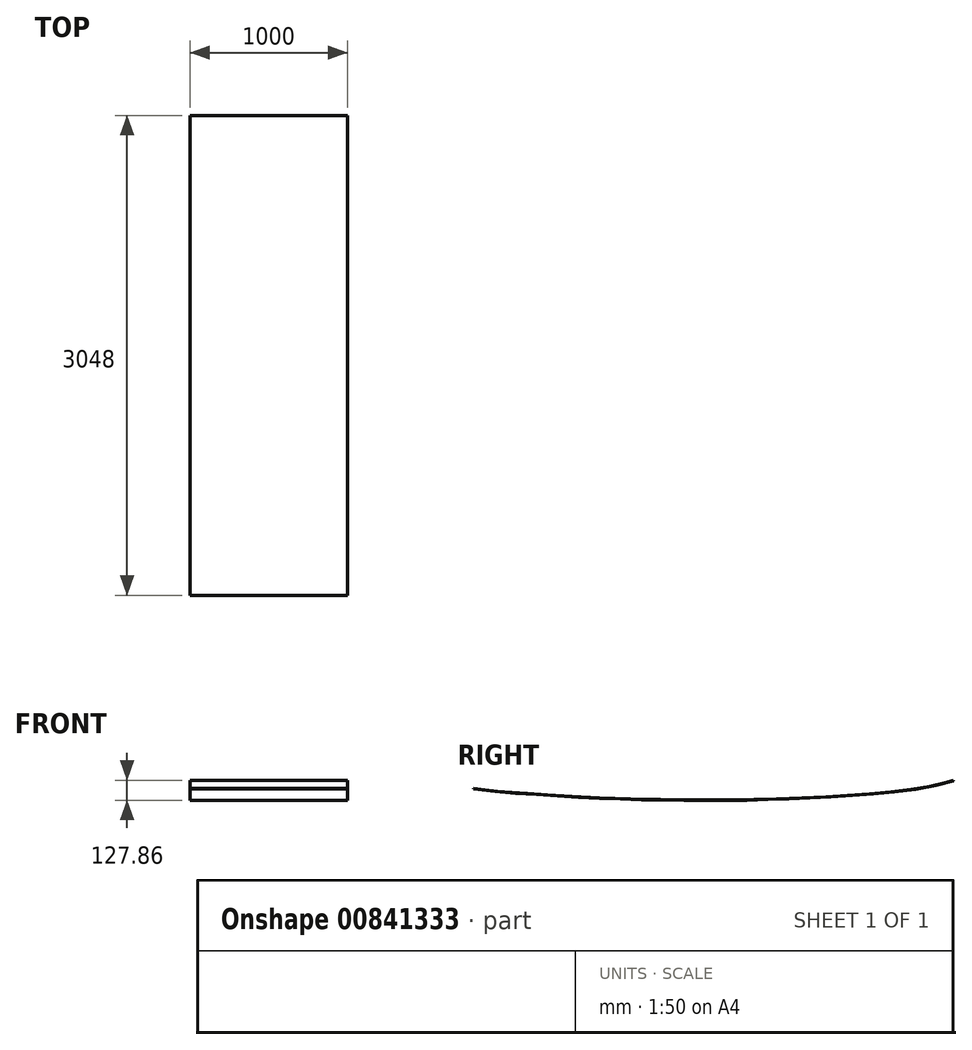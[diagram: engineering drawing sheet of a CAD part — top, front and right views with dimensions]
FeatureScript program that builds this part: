
annotation { "Feature Type Name" : "Feature", "Feature Type Description" : "" }
export const myFeature = defineFeature(function(context is Context, id is Id, definition is map)
    precondition{}
    {
        {
            var Q0;
            Q0=qCreatedBy(makeId("Right.planeOp"),FACE);
            var sketch = newSketch(context, id + "F0", { "sketchPlane" : qUnion([Q0])});
            skFitSpline(sketch, "E0", {"points": [v(-1524, 72) * mm, v(-1424, 61) * mm, v(-1324, 51) * mm, v(-1224, 43) * mm, v(-1124, 37) * mm, v(-1024, 30) * mm, v(-924, 24) * mm, v(-824, 19) * mm, v(-724, 14) * mm, v(-624, 10) * mm, v(-524, 7) * mm, v(-424, 4) * mm, v(-324, 2) * mm, v(-224, 1) * mm, v(-124, 0) * mm, v(-24, 0) * mm, v(76, 0) * mm, v(176, 1) * mm, v(276, 3) * mm, v(376, 6) * mm, v(476, 9) * mm, v(576, 13) * mm, v(676, 18) * mm, v(776, 24) * mm, v(876, 30) * mm, v(976, 38) * mm, v(1076, 47) * mm, v(1176, 57) * mm, v(1276, 70) * mm, v(1376, 86) * mm, v(1476, 110) * mm, v(1524, 125) * mm], "startDerivative": vector(44.76, -10.57) * mm, "endDerivative": vector(60.2, 24.67) * mm});
            skLineSegment(sketch, "E1", {"start": v(-1524, 0) * mm, "end": v(1524, 0) * mm, "construction": true});
            skLineSegment(sketch, "E2", {"start": v(1524, 125) * mm, "end": v(1523.54, 124.81) * mm, "construction": true});
            skPoint(sketch, "E3", {"position": v(1219, 0) * mm});
            skPoint(sketch, "E4", {"position": v(-1219, 0) * mm});
            skLineSegment(sketch, "E5", {"start": v(-1524, 72) * mm, "end": v(-1523.51, 71.89) * mm, "construction": true});
            skFitSpline(sketch, "E6.0", {"points": [v(-1525.26, 75.2) * mm, v(-1525.15, 75.2) * mm, v(-1524.92, 75.16) * mm, v(-1524.63, 75.12) * mm, v(-1524.4, 75.09) * mm, v(-1524.23, 75.06) * mm, v(-1524.06, 75.04) * mm, v(-1523.91, 75.02) * mm, v(-1523.8, 75) * mm, v(-1523.73, 75) * mm, v(-1523.67, 74.98) * mm, v(-1523.63, 74.98) * mm, v(-1523.6, 74.97) * mm, v(-1523.56, 74.97) * mm, v(-1523.55, 74.96) * mm, v(-1523.53, 74.96) * mm, v(-1523.53, 74.96) * mm, v(-1523.53, 74.96) * mm, v(-1523.51, 74.96) * mm, v(-1523.47, 74.95) * mm, v(-1523.39, 74.94) * mm, v(-1523.25, 74.93) * mm, v(-1523.04, 74.9) * mm, v(-1522.7, 74.86) * mm, v(-1522.28, 74.81) * mm, v(-1521.63, 74.74) * mm, v(-1520.65, 74.63) * mm, v(-1519.2, 74.46) * mm, v(-1517.5, 74.27) * mm, v(-1515.57, 74.05) * mm, v(-1512.68, 73.73) * mm, v(-1508.53, 73.27) * mm, v(-1502.8, 72.63) * mm, v(-1494.26, 71.68) * mm, v(-1482.18, 70.35) * mm, v(-1466.2, 68.6) * mm, v(-1452.33, 67.08) * mm, v(-1441.27, 65.88) * mm, v(-1433.11, 65) * mm, v(-1425.17, 64.14) * mm, v(-1417.55, 63.33) * mm, v(-1410.26, 62.55) * mm, v(-1403.27, 61.81) * mm, v(-1396.54, 61.1) * mm, v(-1387.88, 60.2) * mm, v(-1377.6, 59.15) * mm, v(-1365.91, 57.98) * mm, v(-1354.65, 56.87) * mm, v(-1343.62, 55.82) * mm, v(-1334.43, 54.96) * mm, v(-1326.98, 54.28) * mm, v(-1319.42, 53.6) * mm, v(-1309.75, 52.74) * mm, v(-1297.85, 51.7) * mm, v(-1285.7, 50.67) * mm, v(-1273.38, 49.66) * mm, v(-1260.92, 48.68) * mm, v(-1248.4, 47.73) * mm, v(-1235.85, 46.82) * mm, v(-1223.36, 45.96) * mm, v(-1210.96, 45.15) * mm, v(-1198.64, 44.4) * mm, v(-1182.3, 43.43) * mm, v(-1161.98, 42.28) * mm, v(-1141.73, 41.1) * mm, v(-1125.51, 40.1) * mm, v(-1109.26, 39.05) * mm, v(-1088.9, 37.64) * mm, v(-1064.41, 35.87) * mm, v(-1039.9, 34.1) * mm, v(-1015.42, 32.4) * mm, v(-990.96, 30.83) * mm, v(-958.36, 28.86) * mm, v(-917.61, 26.63) * mm, v(-876.83, 24.6) * mm, v(-844.19, 23) * mm, v(-811.54, 21.39) * mm, v(-770.75, 19.28) * mm, v(-721.82, 16.85) * mm, v(-672.88, 14.74) * mm, v(-623.94, 12.95) * mm, v(-574.98, 11.47) * mm, v(-526, 10.09) * mm, v(-477.03, 8.54) * mm, v(-428.07, 7.06) * mm, v(-379.12, 5.88) * mm, v(-338.32, 5.17) * mm, v(-305.68, 4.77) * mm, v(-281.2, 4.53) * mm, v(-256.7, 4.31) * mm, v(-232.22, 4.1) * mm, v(-207.72, 3.83) * mm, v(-183.23, 3.53) * mm, v(-158.75, 3.26) * mm, v(-134.27, 3.04) * mm, v(-109.79, 2.93) * mm, v(-85.3, 2.92) * mm, v(-60.82, 2.95) * mm, v(-36.33, 3) * mm, v(-11.83, 3) * mm, v(20.82, 2.96) * mm, v(53.47, 2.92) * mm, v(86.11, 3.03) * mm, v(118.75, 3.26) * mm, v(151.4, 3.64) * mm, v(184.04, 4.12) * mm, v(216.68, 4.66) * mm, v(249.32, 5.32) * mm, v(281.95, 6.15) * mm, v(306.43, 6.85) * mm, v(330.91, 7.6) * mm, v(355.4, 8.37) * mm, v(379.89, 9.12) * mm, v(412.54, 10.07) * mm, v(445.18, 11) * mm, v(477.81, 12.05) * mm, v(510.44, 13.22) * mm, v(543.07, 14.55) * mm, v(575.7, 15.98) * mm, v(608.33, 17.48) * mm, v(640.96, 19.08) * mm, v(673.57, 20.85) * mm, v(698.03, 22.28) * mm, v(722.5, 23.76) * mm, v(746.96, 25.26) * mm, v(771.43, 26.75) * mm, v(795.91, 28.16) * mm, v(820.38, 29.55) * mm, v(844.84, 30.98) * mm, v(869.3, 32.52) * mm, v(893.73, 34.24) * mm, v(918.16, 36.12) * mm, v(942.6, 38.13) * mm, v(967.04, 40.22) * mm, v(991.48, 42.37) * mm, v(1015.91, 44.54) * mm, v(1040.35, 46.75) * mm, v(1064.79, 48.98) * mm, v(1089.23, 51.23) * mm, v(1113.66, 53.52) * mm, v(1138.08, 55.92) * mm, v(1158.41, 58.05) * mm, v(1174.66, 59.86) * mm, v(1190.91, 61.75) * mm, v(1211.21, 64.25) * mm, v(1235.57, 67.43) * mm, v(1255.88, 70.2) * mm, v(1272.13, 72.48) * mm, v(1288.4, 74.78) * mm, v(1308.72, 77.73) * mm, v(1333.07, 81.49) * mm, v(1353.3, 84.87) * mm, v(1369.4, 87.79) * mm, v(1385.47, 90.86) * mm, v(1401.47, 94.18) * mm, v(1417.46, 97.78) * mm, v(1429.46, 100.62) * mm, v(1441.49, 103.62) * mm, v(1451.53, 106.26) * mm, v(1459.6, 108.45) * mm, v(1465.65, 110.14) * mm, v(1470.7, 111.59) * mm, v(1474.76, 112.76) * mm, v(1478.83, 113.96) * mm, v(1483.9, 115.47) * mm, v(1491.85, 117.88) * mm, v(1499.39, 120.22) * mm, v(1506.15, 122.36) * mm, v(1510.74, 123.82) * mm, v(1514.75, 125.11) * mm, v(1517.54, 126.02) * mm, v(1519.38, 126.62) * mm, v(1520.57, 127.01) * mm, v(1521.38, 127.28) * mm, v(1521.91, 127.46) * mm, v(1522.25, 127.57) * mm, v(1522.53, 127.67) * mm, v(1522.71, 127.73) * mm, v(1522.83, 127.77) * mm, v(1522.9, 127.79) * mm, v(1522.93, 127.8) * mm, v(1522.94, 127.8) * mm, v(1522.94, 127.8) * mm, v(1522.95, 127.8) * mm, v(1522.96, 127.81) * mm, v(1522.97, 127.82) * mm, v(1523, 127.83) * mm, v(1523.02, 127.84) * mm, v(1523.06, 127.85) * mm, v(1523.1, 127.87) * mm, v(1523.17, 127.89) * mm, v(1523.27, 127.93) * mm, v(1523.4, 127.97) * mm, v(1523.54, 128.02) * mm, v(1523.69, 128.08) * mm, v(1523.88, 128.15) * mm, v(1524.13, 128.24) * mm, v(1524.32, 128.3) * mm, v(1524.42, 128.34) * mm]});
            skLineSegment(sketch, "E7", {"start": v(1524, 125) * mm, "end": v(1522.86, 127.78) * mm});
            skLineSegment(sketch, "E8", {"start": v(-1524, 72) * mm, "end": v(-1523.3, 74.93) * mm});
            skSolve(sketch);
        }
        {
            var Q0;
            Q0=qSketchRegion(id+"F0",true);
            extrude(context, id + "F1", {"entities" : qUnion([Q0]), "depth" : 1000 * mm, "offsetDistance" : 25 * mm});
        }
    });
